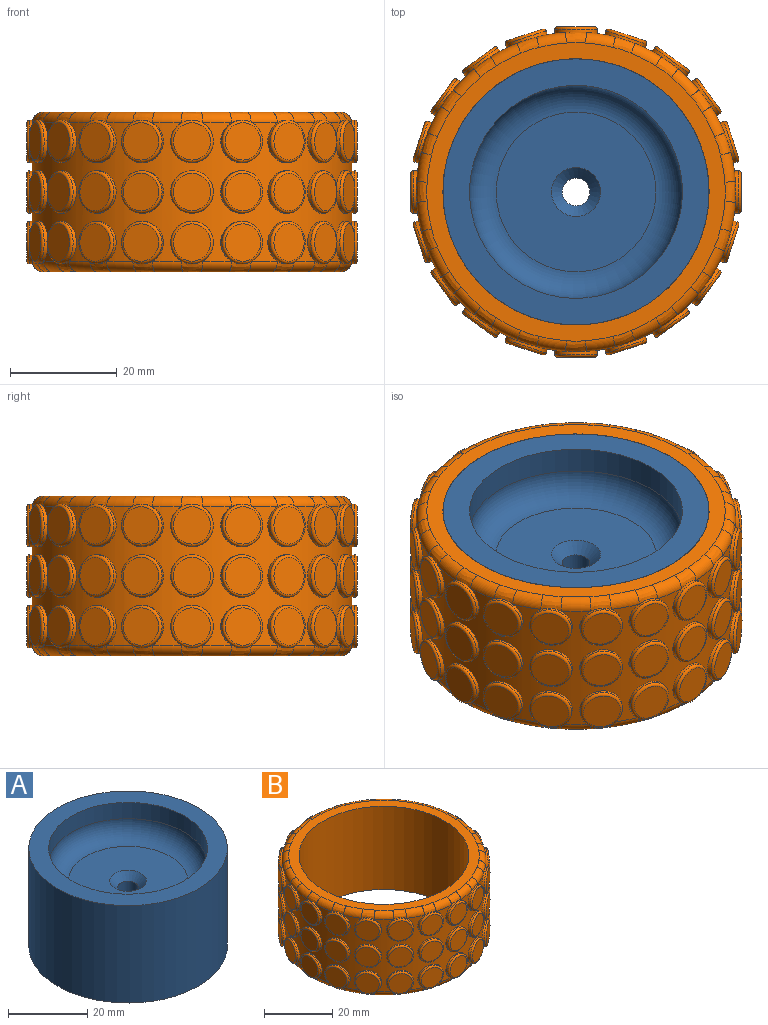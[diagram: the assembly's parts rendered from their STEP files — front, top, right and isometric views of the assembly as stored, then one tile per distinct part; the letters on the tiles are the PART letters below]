
ASSEMBLY  parts=2 mates=1
PART A: 12 faces, bbox 50x50x30 mm
  f0: plane 50x50mm, normal (0,0,1), area 706.9mm2, adj f1,f5
  f1: cylinder r=25mm len=50mm, axis (0,0,1), area 4712.4mm2, adj f0,f2
  f2: plane 50x50mm, normal (0,0,-1), area 706.9mm2, adj f1,f4
  f3: cylinder r=2.6mm len=6mm, axis (0,0,1), area 98mm2, adj f8,f9
  f4: cylinder r=20mm len=40mm, axis (0,0,1), area 628.3mm2, adj f2,f7
  f5: cylinder r=20mm len=40mm, axis (0,0,1), area 628.3mm2, adj f0,f6
  f6: torus R=15mm, axis (0,0,1), area 897.3mm2, adj f5,f11
  f7: torus R=15mm, axis (0,0,1), area 897.3mm2, adj f4,f10
  f8: cone r=4.6mm half-angle=45deg, axis (0,0,-1), area 64mm2, adj f3,f10
  f9: cone r=2.6mm half-angle=45deg, axis (0,0,1), area 64mm2, adj f3,f11
  f10: plane 30x30mm, normal (0,0,-1), area 640.4mm2, adj f7,f8
  f11: plane 30x30mm, normal (0,0,1), area 640.4mm2, adj f6,f9
PART B: 264 faces, bbox 62x62x30 mm
  f0: bspline ~4.18x3.06mm, area 10.6mm2, adj f1,f2,f160,f183
  f1: torus R=28mm, axis (0,0,1), area 17mm2, adj f0,f3,f181,f183
  f2: torus R=28mm, axis (0,0,1), area 17mm2, adj f0,f4,f181,f183
  f3: bspline ~3.87x2.06mm, area 10.6mm2, adj f1,f5,f165,f183
  f4: bspline ~4.2x3.82mm, area 10.6mm2, adj f2,f6,f155,f183
  f5: torus R=28mm, axis (0,0,1), area 17mm2, adj f3,f7,f181,f183
  f6: torus R=28mm, axis (0,0,1), area 17mm2, adj f4,f8,f181,f183
  f7: bspline ~4.18x3.06mm, area 10.6mm2, adj f5,f9,f170,f183
  f8: bspline ~4.2x3.82mm, area 10.6mm2, adj f6,f10,f150,f183
  f9: torus R=28mm, axis (0,0,1), area 17mm2, adj f7,f11,f181,f183
  f10: torus R=28mm, axis (0,0,1), area 17mm2, adj f8,f12,f181,f183
  f11: bspline ~4.2x3.82mm, area 10.6mm2, adj f9,f13,f175,f183
  f12: bspline ~4.18x3.06mm, area 10.6mm2, adj f10,f14,f145,f183
  f13: torus R=28mm, axis (0,0,1), area 17mm2, adj f11,f15,f181,f183
  f14: torus R=28mm, axis (0,0,1), area 17mm2, adj f12,f16,f181,f183
  f15: bspline ~4.2x3.82mm, area 10.6mm2, adj f13,f17,f80,f183
  f16: bspline ~3.87x2.06mm, area 10.6mm2, adj f14,f18,f140,f183
  f17: torus R=28mm, axis (0,0,1), area 17mm2, adj f15,f19,f181,f183
  f18: torus R=28mm, axis (0,0,1), area 17mm2, adj f16,f20,f181,f183
  f19: bspline ~4.18x3.06mm, area 10.6mm2, adj f17,f21,f85,f183
  f20: bspline ~4.18x3.06mm, area 10.6mm2, adj f18,f22,f135,f183
  f21: torus R=28mm, axis (0,0,1), area 17mm2, adj f19,f23,f181,f183
  f22: torus R=28mm, axis (0,0,1), area 17mm2, adj f20,f24,f181,f183
  f23: bspline ~3.87x2.06mm, area 10.6mm2, adj f21,f25,f90,f183
  f24: bspline ~4.2x3.82mm, area 10.6mm2, adj f22,f26,f130,f183
  f25: torus R=28mm, axis (0,0,1), area 17mm2, adj f23,f27,f181,f183
  f26: torus R=28mm, axis (0,0,1), area 17mm2, adj f24,f28,f181,f183
  f27: bspline ~4.18x3.06mm, area 10.6mm2, adj f25,f29,f95,f183
  f28: bspline ~4.2x3.82mm, area 10.6mm2, adj f26,f30,f125,f183
  f29: torus R=28mm, axis (0,0,1), area 17mm2, adj f27,f31,f181,f183
  f30: torus R=28mm, axis (0,0,1), area 17mm2, adj f28,f32,f181,f183
  f31: bspline ~4.2x3.82mm, area 10.6mm2, adj f29,f33,f100,f183
  f32: bspline ~4.18x3.06mm, area 10.6mm2, adj f30,f34,f120,f183
  f33: torus R=28mm, axis (0,0,1), area 17mm2, adj f31,f35,f181,f183
  f34: torus R=28mm, axis (0,0,1), area 17mm2, adj f32,f36,f181,f183
  f35: bspline ~4.2x3.82mm, area 10.6mm2, adj f33,f37,f105,f183
  f36: bspline ~3.87x2.06mm, area 10.6mm2, adj f34,f38,f115,f183
  f37: torus R=28mm, axis (0,0,1), area 17mm2, adj f35,f39,f181,f183
  f38: torus R=28mm, axis (0,0,1), area 17mm2, adj f36,f39,f181,f183
  f39: bspline ~4.18x3.06mm, area 10.6mm2, adj f37,f38,f110,f183
  f40: bspline ~4.18x3.06mm, area 10.6mm2, adj f41,f42,f162,f182
  f41: torus R=28mm, axis (0,0,1), area 17mm2, adj f40,f43,f181,f182
  f42: torus R=28mm, axis (0,0,1), area 17mm2, adj f40,f44,f181,f182
  f43: bspline ~3.87x2.06mm, area 10.6mm2, adj f41,f45,f167,f182
  f44: bspline ~4.2x3.82mm, area 10.6mm2, adj f42,f46,f157,f182
  f45: torus R=28mm, axis (0,0,1), area 17mm2, adj f43,f47,f181,f182
  f46: torus R=28mm, axis (0,0,1), area 17mm2, adj f44,f48,f181,f182
  f47: bspline ~4.18x3.06mm, area 10.6mm2, adj f45,f49,f172,f182
  f48: bspline ~4.2x3.82mm, area 10.6mm2, adj f46,f50,f152,f182
  f49: torus R=28mm, axis (0,0,1), area 17mm2, adj f47,f51,f181,f182
  f50: torus R=28mm, axis (0,0,1), area 17mm2, adj f48,f52,f181,f182
  f51: bspline ~4.2x3.82mm, area 10.6mm2, adj f49,f53,f177,f182
  f52: bspline ~4.18x3.06mm, area 10.6mm2, adj f50,f54,f147,f182
  f53: torus R=28mm, axis (0,0,1), area 17mm2, adj f51,f55,f181,f182
  f54: torus R=28mm, axis (0,0,1), area 17mm2, adj f52,f56,f181,f182
  f55: bspline ~4.2x3.82mm, area 10.6mm2, adj f53,f57,f82,f182
  f56: bspline ~3.87x2.06mm, area 10.6mm2, adj f54,f58,f142,f182
  f57: torus R=28mm, axis (0,0,1), area 17mm2, adj f55,f59,f181,f182
  f58: torus R=28mm, axis (0,0,1), area 17mm2, adj f56,f60,f181,f182
  f59: bspline ~4.18x3.06mm, area 10.6mm2, adj f57,f61,f87,f182
  f60: bspline ~4.18x3.06mm, area 10.6mm2, adj f58,f62,f137,f182
  f61: torus R=28mm, axis (0,0,1), area 17mm2, adj f59,f63,f181,f182
  f62: torus R=28mm, axis (0,0,1), area 17mm2, adj f60,f64,f181,f182
  f63: bspline ~3.87x2.06mm, area 10.6mm2, adj f61,f65,f92,f182
  f64: bspline ~4.2x3.82mm, area 10.6mm2, adj f62,f66,f132,f182
  f65: torus R=28mm, axis (0,0,1), area 17mm2, adj f63,f67,f181,f182
  f66: torus R=28mm, axis (0,0,1), area 17mm2, adj f64,f68,f181,f182
  f67: bspline ~4.18x3.06mm, area 10.6mm2, adj f65,f69,f97,f182
  f68: bspline ~4.2x3.82mm, area 10.6mm2, adj f66,f70,f127,f182
  f69: torus R=28mm, axis (0,0,1), area 17mm2, adj f67,f71,f181,f182
  f70: torus R=28mm, axis (0,0,1), area 17mm2, adj f68,f72,f181,f182
  f71: bspline ~4.2x3.82mm, area 10.6mm2, adj f69,f73,f102,f182
  f72: bspline ~4.18x3.06mm, area 10.6mm2, adj f70,f74,f122,f182
  f73: torus R=28mm, axis (0,0,1), area 17mm2, adj f71,f75,f181,f182
  f74: torus R=28mm, axis (0,0,1), area 17mm2, adj f72,f76,f181,f182
  f75: bspline ~4.2x3.82mm, area 10.6mm2, adj f73,f77,f107,f182
  f76: bspline ~3.87x2.06mm, area 10.6mm2, adj f74,f78,f117,f182
  f77: torus R=28mm, axis (0,0,1), area 17mm2, adj f75,f79,f181,f182
  f78: torus R=28mm, axis (0,0,1), area 17mm2, adj f76,f79,f181,f182
  f79: bspline ~4.18x3.06mm, area 10.6mm2, adj f77,f78,f112,f182
  f80: cylinder r=4mm len=8mm, axis (0.59,0.81,0), area 14mm2, adj f15,f180,f181
  f81: plane 7x5.66mm, normal (0.59,0.81,0), area 38.5mm2, adj f226
  f82: cylinder r=4mm len=8mm, axis (0.59,0.81,0), area 13.5mm2, adj f55,f181,f226
  f83: plane 7x5.66mm, normal (0.59,0.81,0), area 38.5mm2, adj f227
  f84: cylinder r=4mm len=8mm, axis (0.59,0.81,0), area 15.9mm2, adj f181,f227
  f85: cylinder r=4mm len=8mm, axis (0.31,0.95,0), area 14mm2, adj f19,f181,f187
  f86: plane 7x6.66mm, normal (0.31,0.95,0), area 38.5mm2, adj f186
  f87: cylinder r=4mm len=8mm, axis (0.31,0.95,0), area 13.5mm2, adj f59,f181,f186
  f88: plane 7x6.66mm, normal (0.31,0.95,0), area 38.5mm2, adj f185
  f89: cylinder r=4mm len=8mm, axis (0.31,0.95,0), area 15.9mm2, adj f181,f185
  f90: cylinder r=4mm len=8mm, axis (0,1,0), area 14mm2, adj f23,f181,f261
  f91: plane 7x7mm, normal (0,1,0), area 38.5mm2, adj f262
  f92: cylinder r=4mm len=8mm, axis (0,1,0), area 13.5mm2, adj f63,f181,f262
  f93: plane 7x7mm, normal (0,1,0), area 38.5mm2, adj f263
  f94: cylinder r=4mm len=8mm, axis (0,1,0), area 15.9mm2, adj f181,f263
  f95: cylinder r=4mm len=8mm, axis (-0.31,0.95,0), area 14mm2, adj f27,f181,f192
  f96: plane 7x6.66mm, normal (-0.31,0.95,0), area 38.5mm2, adj f190
  f97: cylinder r=4mm len=8mm, axis (-0.31,0.95,0), area 13.5mm2, adj f67,f181,f190
  f98: plane 7x6.66mm, normal (-0.31,0.95,0), area 38.5mm2, adj f189
  f99: cylinder r=4mm len=8mm, axis (-0.31,0.95,0), area 15.9mm2, adj f181,f189
  f100: cylinder r=4mm len=8mm, axis (-0.59,0.81,0), area 14mm2, adj f31,f181,f257
  f101: plane 7x5.66mm, normal (-0.59,0.81,0), area 38.5mm2, adj f258
  f102: cylinder r=4mm len=8mm, axis (-0.59,0.81,0), area 13.5mm2, adj f71,f181,f258
  f103: plane 7x5.66mm, normal (-0.59,0.81,0), area 38.5mm2, adj f259
  f104: cylinder r=4mm len=8mm, axis (-0.59,0.81,0), area 15.9mm2, adj f181,f259
  f105: cylinder r=4mm len=8mm, axis (-0.81,0.59,0), area 14mm2, adj f35,f181,f196
  f106: plane 7x5.66mm, normal (-0.81,0.59,0), area 38.5mm2, adj f194
  f107: cylinder r=4mm len=8mm, axis (-0.81,0.59,0), area 13.5mm2, adj f75,f181,f194
  f108: plane 7x5.66mm, normal (-0.81,0.59,0), area 38.5mm2, adj f193
  f109: cylinder r=4mm len=8mm, axis (-0.81,0.59,0), area 15.9mm2, adj f181,f193
  f110: cylinder r=4mm len=8mm, axis (-0.95,0.31,0), area 14mm2, adj f39,f181,f253
  f111: plane 7x6.66mm, normal (-0.95,0.31,0), area 38.5mm2, adj f254
  f112: cylinder r=4mm len=8mm, axis (-0.95,0.31,0), area 13.7mm2, adj f79,f181,f254
  f113: plane 7x6.66mm, normal (-0.95,0.31,0), area 38.5mm2, adj f255
  f114: cylinder r=4mm len=8mm, axis (-0.95,0.31,0), area 13.6mm2, adj f181,f255
  f115: cylinder r=4mm len=8mm, axis (-1,0,0), area 14mm2, adj f36,f181,f200
  f116: plane 7x7mm, normal (-1,0,0), area 38.5mm2, adj f198
  f117: cylinder r=4mm len=8mm, axis (-1,0,0), area 13.5mm2, adj f76,f181,f198
  f118: plane 7x7mm, normal (-1,0,0), area 38.5mm2, adj f197
  f119: cylinder r=4mm len=8mm, axis (-1,0,0), area 15.9mm2, adj f181,f197
  f120: cylinder r=4mm len=8mm, axis (-0.95,-0.31,0), area 14mm2, adj f32,f181,f249
  f121: plane 7x6.66mm, normal (-0.95,-0.31,0), area 38.5mm2, adj f250
  f122: cylinder r=4mm len=8mm, axis (-0.95,-0.31,0), area 13.5mm2, adj f72,f181,f250
  f123: plane 7x6.66mm, normal (-0.95,-0.31,0), area 38.5mm2, adj f251
  f124: cylinder r=4mm len=8mm, axis (-0.95,-0.31,0), area 15.9mm2, adj f181,f251
  f125: cylinder r=4mm len=8mm, axis (-0.81,-0.59,0), area 14mm2, adj f28,f181,f204
  f126: plane 7x5.66mm, normal (-0.81,-0.59,0), area 38.5mm2, adj f202
  f127: cylinder r=4mm len=8mm, axis (-0.81,-0.59,0), area 13.5mm2, adj f68,f181,f202
  f128: plane 7x5.66mm, normal (-0.81,-0.59,0), area 38.5mm2, adj f201
  f129: cylinder r=4mm len=8mm, axis (-0.81,-0.59,0), area 15.9mm2, adj f181,f201
  f130: cylinder r=4mm len=8mm, axis (-0.59,-0.81,0), area 14mm2, adj f24,f181,f245
  f131: plane 7x5.66mm, normal (-0.59,-0.81,0), area 38.5mm2, adj f246
  f132: cylinder r=4mm len=8mm, axis (-0.59,-0.81,0), area 13.5mm2, adj f64,f181,f246
  f133: plane 7x5.66mm, normal (-0.59,-0.81,0), area 38.5mm2, adj f247
  f134: cylinder r=4mm len=8mm, axis (-0.59,-0.81,0), area 15.9mm2, adj f181,f247
  f135: cylinder r=4mm len=8mm, axis (-0.31,-0.95,0), area 14mm2, adj f20,f181,f208
  f136: plane 7x6.66mm, normal (-0.31,-0.95,0), area 38.5mm2, adj f206
  f137: cylinder r=4mm len=8mm, axis (-0.31,-0.95,0), area 13.5mm2, adj f60,f181,f206
  f138: plane 7x6.66mm, normal (-0.31,-0.95,0), area 38.5mm2, adj f205
  f139: cylinder r=4mm len=8mm, axis (-0.31,-0.95,0), area 15.9mm2, adj f181,f205
  f140: cylinder r=4mm len=8mm, axis (0,-1,0), area 14mm2, adj f16,f181,f241
  f141: plane 7x7mm, normal (0,-1,0), area 38.5mm2, adj f242
  f142: cylinder r=4mm len=8mm, axis (0,-1,0), area 13.5mm2, adj f56,f181,f242
  f143: plane 7x7mm, normal (0,-1,0), area 38.5mm2, adj f243
  f144: cylinder r=4mm len=8mm, axis (0,-1,0), area 15.9mm2, adj f181,f243
  f145: cylinder r=4mm len=8mm, axis (0.31,-0.95,0), area 14mm2, adj f12,f181,f212
  f146: plane 7x6.66mm, normal (0.31,-0.95,0), area 38.5mm2, adj f210
  f147: cylinder r=4mm len=8mm, axis (0.31,-0.95,0), area 13.5mm2, adj f52,f181,f210
  f148: plane 7x6.66mm, normal (0.31,-0.95,0), area 38.5mm2, adj f209
  f149: cylinder r=4mm len=8mm, axis (0.31,-0.95,0), area 15.9mm2, adj f181,f209
  f150: cylinder r=4mm len=8mm, axis (0.59,-0.81,0), area 14mm2, adj f8,f181,f237
  f151: plane 7x5.66mm, normal (0.59,-0.81,0), area 38.5mm2, adj f238
  f152: cylinder r=4mm len=8mm, axis (0.59,-0.81,0), area 13.5mm2, adj f48,f181,f238
  f153: plane 7x5.66mm, normal (0.59,-0.81,0), area 38.5mm2, adj f239
  f154: cylinder r=4mm len=8mm, axis (0.59,-0.81,0), area 15.9mm2, adj f181,f239
  f155: cylinder r=4mm len=8mm, axis (0.81,-0.59,0), area 14mm2, adj f4,f181,f216
  f156: plane 7x5.66mm, normal (0.81,-0.59,0), area 38.5mm2, adj f214
  f157: cylinder r=4mm len=8mm, axis (0.81,-0.59,0), area 13.5mm2, adj f44,f181,f214
  f158: plane 7x5.66mm, normal (0.81,-0.59,0), area 38.5mm2, adj f213
  f159: cylinder r=4mm len=8mm, axis (0.81,-0.59,0), area 15.9mm2, adj f181,f213
  f160: cylinder r=4mm len=8mm, axis (0.95,-0.31,0), area 14mm2, adj f0,f181,f233
  f161: plane 7x6.66mm, normal (0.95,-0.31,0), area 38.5mm2, adj f234
  f162: cylinder r=4mm len=8mm, axis (0.95,-0.31,0), area 13.5mm2, adj f40,f181,f234
  f163: plane 7x6.66mm, normal (0.95,-0.31,0), area 38.5mm2, adj f235
  f164: cylinder r=4mm len=8mm, axis (0.95,-0.31,0), area 15.9mm2, adj f181,f235
  f165: cylinder r=4mm len=8mm, axis (1,0,0), area 14mm2, adj f3,f181,f220
  f166: plane 7x7mm, normal (1,0,0), area 38.5mm2, adj f218
  f167: cylinder r=4mm len=8mm, axis (1,0,0), area 13.5mm2, adj f43,f181,f218
  f168: plane 7x7mm, normal (1,0,0), area 38.5mm2, adj f217
  f169: cylinder r=4mm len=8mm, axis (1,0,0), area 15.9mm2, adj f181,f217
  f170: cylinder r=4mm len=8mm, axis (0.95,0.31,0), area 14mm2, adj f7,f181,f229
  f171: plane 7x6.66mm, normal (0.95,0.31,0), area 38.5mm2, adj f230
  f172: cylinder r=4mm len=8mm, axis (0.95,0.31,0), area 13.5mm2, adj f47,f181,f230
  f173: plane 7x6.66mm, normal (0.95,0.31,0), area 38.5mm2, adj f231
  f174: cylinder r=4mm len=8mm, axis (0.95,0.31,0), area 15.9mm2, adj f181,f231
  f175: cylinder r=4mm len=8mm, axis (0.81,0.59,0), area 14mm2, adj f11,f181,f224
  f176: plane 7x5.66mm, normal (0.81,0.59,0), area 38.5mm2, adj f222
  f177: cylinder r=4mm len=8mm, axis (0.81,0.59,0), area 13.5mm2, adj f51,f181,f222
  f178: plane 7x5.66mm, normal (0.81,0.59,0), area 38.5mm2, adj f221
  f179: cylinder r=4mm len=8mm, axis (0.81,0.59,0), area 15.9mm2, adj f181,f221
  f180: torus R=3.5mm, axis (-0.59,-0.81,0), area 18.8mm2, adj f80,f225
  f181: cylinder r=30mm len=60mm, axis (0,0,1), area 1930.5mm2, adj f1,f2,f5,f6,f9,f10,f13,f14
  f182: plane 56.13x56.13mm, normal (0,0,1), area 501.9mm2, adj f40,f41,f42,f43,f44,f45,f46,f47
  f183: plane 56.13x56.13mm, normal (0,0,-1), area 501.9mm2, adj f0,f1,f2,f3,f4,f5,f6,f7
  f184: cylinder r=25mm len=50mm, axis (0,0,1), area 4712.4mm2, adj f182,f183
  f185: torus R=3.5mm, axis (-0.31,-0.95,0), area 18.8mm2, adj f88,f89
  f186: torus R=3.5mm, axis (-0.31,-0.95,0), area 18.8mm2, adj f86,f87
  f187: torus R=3.5mm, axis (-0.31,-0.95,0), area 18.8mm2, adj f85,f188
  f188: plane 7x6.66mm, normal (0.31,0.95,0), area 38.5mm2, adj f187
  f189: torus R=3.5mm, axis (0.31,-0.95,0), area 18.8mm2, adj f98,f99
  f190: torus R=3.5mm, axis (0.31,-0.95,0), area 18.8mm2, adj f96,f97
  f191: plane 7x6.66mm, normal (-0.31,0.95,0), area 38.5mm2, adj f192
  f192: torus R=3.5mm, axis (0.31,-0.95,0), area 18.8mm2, adj f95,f191
  f193: torus R=3.5mm, axis (0.81,-0.59,0), area 18.8mm2, adj f108,f109
  f194: torus R=3.5mm, axis (0.81,-0.59,0), area 18.8mm2, adj f106,f107
  f195: plane 7x5.66mm, normal (-0.81,0.59,0), area 38.5mm2, adj f196
  f196: torus R=3.5mm, axis (0.81,-0.59,0), area 18.8mm2, adj f105,f195
  f197: torus R=3.5mm, axis (1,0,0), area 18.8mm2, adj f118,f119
  f198: torus R=3.5mm, axis (1,0,0), area 18.8mm2, adj f116,f117
  f199: plane 7x7mm, normal (-1,0,0), area 38.5mm2, adj f200
  f200: torus R=3.5mm, axis (1,0,0), area 18.8mm2, adj f115,f199
  f201: torus R=3.5mm, axis (0.81,0.59,0), area 18.8mm2, adj f128,f129
  f202: torus R=3.5mm, axis (0.81,0.59,0), area 18.8mm2, adj f126,f127
  f203: plane 7x5.66mm, normal (-0.81,-0.59,0), area 38.5mm2, adj f204
  f204: torus R=3.5mm, axis (0.81,0.59,0), area 18.8mm2, adj f125,f203
  f205: torus R=3.5mm, axis (0.31,0.95,0), area 18.8mm2, adj f138,f139
  f206: torus R=3.5mm, axis (0.31,0.95,0), area 18.8mm2, adj f136,f137
  f207: plane 7x6.66mm, normal (-0.31,-0.95,0), area 38.5mm2, adj f208
  f208: torus R=3.5mm, axis (0.31,0.95,0), area 18.8mm2, adj f135,f207
  f209: torus R=3.5mm, axis (-0.31,0.95,0), area 18.8mm2, adj f148,f149
  f210: torus R=3.5mm, axis (-0.31,0.95,0), area 18.8mm2, adj f146,f147
  f211: plane 7x6.66mm, normal (0.31,-0.95,0), area 38.5mm2, adj f212
  f212: torus R=3.5mm, axis (-0.31,0.95,0), area 18.8mm2, adj f145,f211
  f213: torus R=3.5mm, axis (-0.81,0.59,0), area 18.8mm2, adj f158,f159
  f214: torus R=3.5mm, axis (-0.81,0.59,0), area 18.8mm2, adj f156,f157
  f215: plane 7x5.66mm, normal (0.81,-0.59,0), area 38.5mm2, adj f216
  f216: torus R=3.5mm, axis (-0.81,0.59,0), area 18.8mm2, adj f155,f215
  f217: torus R=3.5mm, axis (-1,0,0), area 18.8mm2, adj f168,f169
  f218: torus R=3.5mm, axis (-1,0,0), area 18.8mm2, adj f166,f167
  f219: plane 7x7mm, normal (1,0,0), area 38.5mm2, adj f220
  f220: torus R=3.5mm, axis (-1,0,0), area 18.8mm2, adj f165,f219
  f221: torus R=3.5mm, axis (-0.81,-0.59,0), area 18.8mm2, adj f178,f179
  f222: torus R=3.5mm, axis (-0.81,-0.59,0), area 18.8mm2, adj f176,f177
  f223: plane 7x5.66mm, normal (0.81,0.59,0), area 38.5mm2, adj f224
  f224: torus R=3.5mm, axis (-0.81,-0.59,0), area 18.8mm2, adj f175,f223
  f225: plane 7x5.66mm, normal (0.59,0.81,0), area 38.5mm2, adj f180
  f226: torus R=3.5mm, axis (-0.59,-0.81,0), area 18.8mm2, adj f81,f82
  f227: torus R=3.5mm, axis (-0.59,-0.81,0), area 18.8mm2, adj f83,f84
  f228: plane 7x6.66mm, normal (0.95,0.31,0), area 38.5mm2, adj f229
  f229: torus R=3.5mm, axis (-0.95,-0.31,0), area 18.8mm2, adj f170,f228
  f230: torus R=3.5mm, axis (-0.95,-0.31,0), area 18.8mm2, adj f171,f172
  f231: torus R=3.5mm, axis (-0.95,-0.31,0), area 18.8mm2, adj f173,f174
  f232: plane 7x6.66mm, normal (0.95,-0.31,0), area 38.5mm2, adj f233
  f233: torus R=3.5mm, axis (-0.95,0.31,0), area 18.8mm2, adj f160,f232
  f234: torus R=3.5mm, axis (-0.95,0.31,0), area 18.8mm2, adj f161,f162
  f235: torus R=3.5mm, axis (-0.95,0.31,0), area 18.8mm2, adj f163,f164
  f236: plane 7x5.66mm, normal (0.59,-0.81,0), area 38.5mm2, adj f237
  f237: torus R=3.5mm, axis (-0.59,0.81,0), area 18.8mm2, adj f150,f236
  f238: torus R=3.5mm, axis (-0.59,0.81,0), area 18.8mm2, adj f151,f152
  f239: torus R=3.5mm, axis (-0.59,0.81,0), area 18.8mm2, adj f153,f154
  f240: plane 7x7mm, normal (0,-1,0), area 38.5mm2, adj f241
  f241: torus R=3.5mm, axis (0,1,0), area 18.8mm2, adj f140,f240
  f242: torus R=3.5mm, axis (0,1,0), area 18.8mm2, adj f141,f142
  f243: torus R=3.5mm, axis (0,1,0), area 18.8mm2, adj f143,f144
  f244: plane 7x5.66mm, normal (-0.59,-0.81,0), area 38.5mm2, adj f245
  f245: torus R=3.5mm, axis (0.59,0.81,0), area 18.8mm2, adj f130,f244
  f246: torus R=3.5mm, axis (0.59,0.81,0), area 18.8mm2, adj f131,f132
  f247: torus R=3.5mm, axis (0.59,0.81,0), area 18.8mm2, adj f133,f134
  f248: plane 7x6.66mm, normal (-0.95,-0.31,0), area 38.5mm2, adj f249
  f249: torus R=3.5mm, axis (0.95,0.31,0), area 18.8mm2, adj f120,f248
  f250: torus R=3.5mm, axis (0.95,0.31,0), area 18.8mm2, adj f121,f122
  f251: torus R=3.5mm, axis (0.95,0.31,0), area 18.8mm2, adj f123,f124
  f252: plane 7x6.66mm, normal (-0.95,0.31,0), area 38.5mm2, adj f253
  f253: torus R=3.5mm, axis (0.95,-0.31,0), area 18.8mm2, adj f110,f252
  f254: torus R=3.5mm, axis (0.95,-0.31,0), area 18.8mm2, adj f111,f112
  f255: torus R=3.5mm, axis (0.95,-0.31,0), area 18.8mm2, adj f113,f114
  f256: plane 7x5.66mm, normal (-0.59,0.81,0), area 38.5mm2, adj f257
  f257: torus R=3.5mm, axis (0.59,-0.81,0), area 18.8mm2, adj f100,f256
  f258: torus R=3.5mm, axis (0.59,-0.81,0), area 18.8mm2, adj f101,f102
  f259: torus R=3.5mm, axis (0.59,-0.81,0), area 18.8mm2, adj f103,f104
  f260: plane 7x7mm, normal (0,1,0), area 38.5mm2, adj f261
  f261: torus R=3.5mm, axis (0,-1,0), area 18.8mm2, adj f90,f260
  f262: torus R=3.5mm, axis (0,-1,0), area 18.8mm2, adj f91,f92
  f263: torus R=3.5mm, axis (0,-1,0), area 18.8mm2, adj f93,f94
PLACE A t=(1.92,-9.04,-15.23)mm
PLACE B t=(1.92,-9.04,-15.23)mm
MATE fastened B.f184 <-> A.f1  axis (0,0,1) through (1.92,-9.04,-0.23)mm
